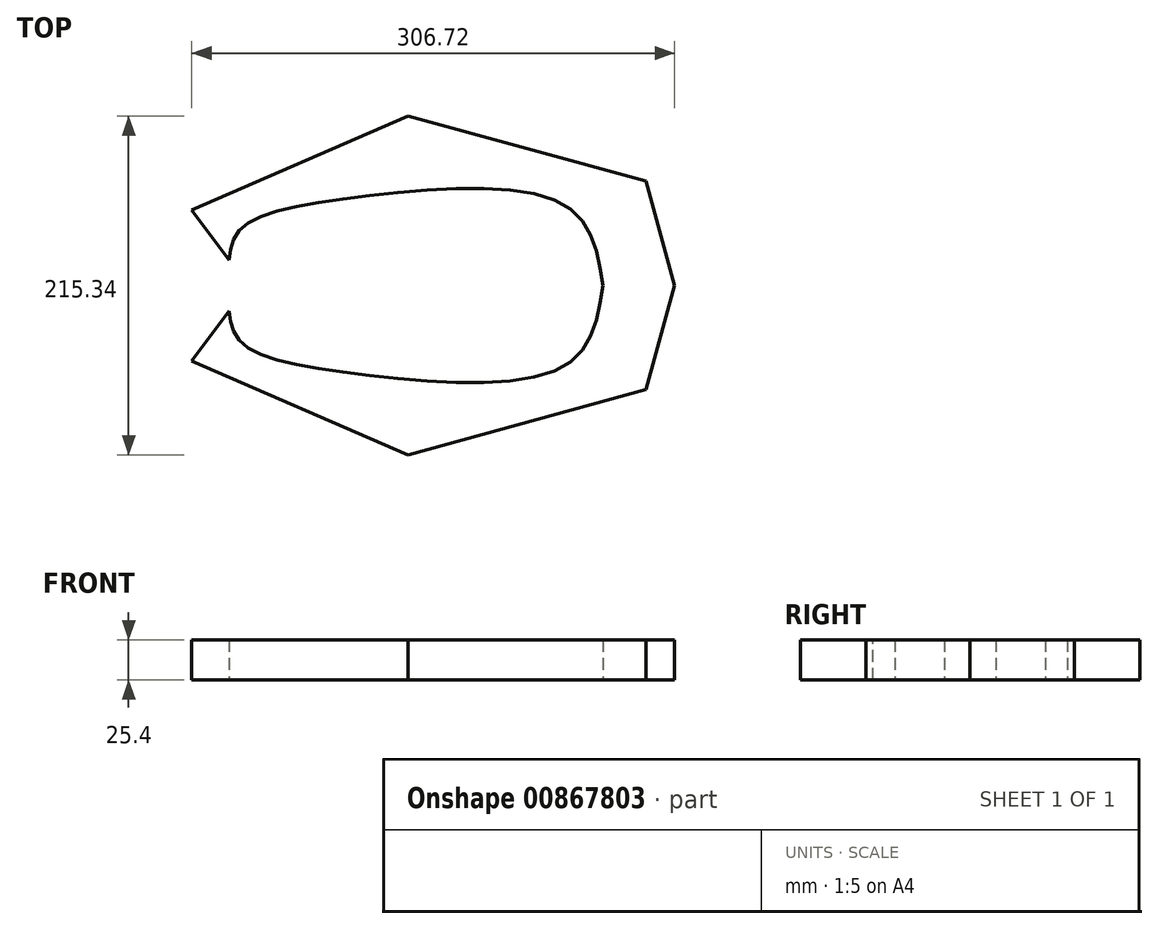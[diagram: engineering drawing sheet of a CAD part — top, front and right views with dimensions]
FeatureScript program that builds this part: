
annotation { "Feature Type Name" : "Feature", "Feature Type Description" : "" }
export const myFeature = defineFeature(function(context is Context, id is Id, definition is map)
    precondition{}
    {
        {
            var Q0;
            Q0=qCreatedBy(makeId("Top.planeOp"),FACE);
            var sketch = newSketch(context, id + "F0", { "sketchPlane" : qUnion([Q0])});
            skFitSpline(sketch, "E0", {"points": [v(-125.05, 16.27) * mm, v(-117.03, 36.33) * mm, v(-45.25, 55.95) * mm, v(88.94, 50.6) * mm, v(112.57, 0) * mm], "startDerivative": vector(23.75, 150.9) * mm, "endDerivative": vector(40.97, -258.61) * mm});
            skFitSpline(sketch, "E1.MirrorCS", {"points": [v(-125.05, -16.27) * mm, v(-117.03, -36.33) * mm, v(-45.25, -55.95) * mm, v(88.94, -50.6) * mm, v(112.57, 0) * mm], "startDerivative": vector(23.75, -150.9) * mm, "endDerivative": vector(40.97, 258.61) * mm});
            skLineSegment(sketch, "E2", {"start": v(-125.05, 16.27) * mm, "end": v(-148.68, 47.93) * mm});
            skLineSegment(sketch, "E3", {"start": v(-148.68, 47.93) * mm, "end": v(-11.37, 107.67) * mm});
            skLineSegment(sketch, "E4", {"start": v(-11.37, 107.67) * mm, "end": v(139.77, 66.2) * mm});
            skLineSegment(sketch, "E5", {"start": v(139.77, 66.2) * mm, "end": v(158.04, 0) * mm});
            skLineSegment(sketch, "E6.MirrorCS", {"start": v(139.77, -66.2) * mm, "end": v(158.04, 0) * mm});
            skLineSegment(sketch, "E7.MirrorCS", {"start": v(-11.37, -107.67) * mm, "end": v(139.77, -66.2) * mm});
            skLineSegment(sketch, "E8.MirrorCS", {"start": v(-125.05, -16.27) * mm, "end": v(-148.68, -47.93) * mm});
            skLineSegment(sketch, "E9.MirrorCS", {"start": v(-148.68, -47.93) * mm, "end": v(-11.37, -107.67) * mm});
            skSolve(sketch);
        }
        {
            var Q0;
            Q0=makeQuery(id+"F0.imprint","IMPRINT",FACE,{"disambiguationData":[TD([[makeQuery(id+"F0.imprint","IMPRINT",EDGE,{"derivedFrom":sQuery(id+"F0.wireOp",EDGE,"E0")}),1.0]])]});
            extrude(context, id + "F1", {"entities" : qUnion([Q0]), "depth" : 25.4 * mm, "offsetDistance" : 25.4 * mm});
        }
    });
